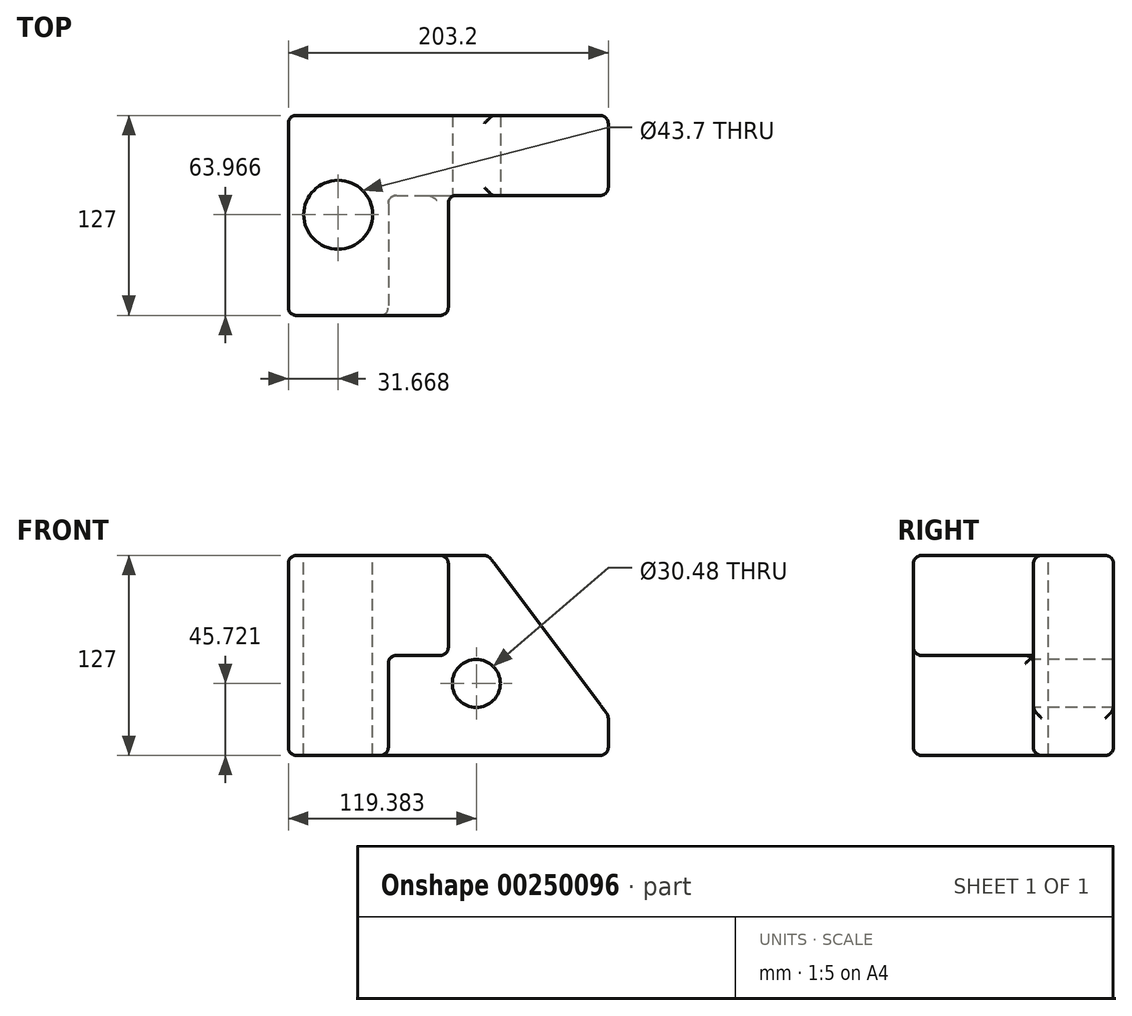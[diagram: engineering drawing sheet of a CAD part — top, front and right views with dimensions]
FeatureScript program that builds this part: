
annotation { "Feature Type Name" : "Feature", "Feature Type Description" : "" }
export const myFeature = defineFeature(function(context is Context, id is Id, definition is map)
    precondition{}
    {
        {
            var Q0;
            Q0=qCreatedBy(makeId("Front.planeOp"),FACE);
            var sketch = newSketch(context, id + "F0", { "sketchPlane" : qUnion([Q0])});
            skLineSegment(sketch, "E0.bottom", {"start": v(-98.38, 50.15) * mm, "end": v(104.82, 50.15) * mm});
            skLineSegment(sketch, "E0.top", {"start": v(-98.38, -76.85) * mm, "end": v(104.82, -76.85) * mm});
            skLineSegment(sketch, "E0.left", {"start": v(-98.38, 50.15) * mm, "end": v(-98.38, -76.85) * mm});
            skLineSegment(sketch, "E0.right", {"start": v(104.82, 50.15) * mm, "end": v(104.82, -76.85) * mm});
            skSolve(sketch);
        }
        {
            var Q0;
            Q0=makeQuery(id+"F0.imprint","IMPRINT",FACE,{"disambiguationData":[TD([[makeQuery(id+"F0.imprint","IMPRINT",EDGE,{"derivedFrom":sQuery(id+"F0.wireOp",EDGE,"E0.bottom")}),-1.0]])]});
            extrude(context, id + "F1", {"entities" : qUnion([Q0]), "depth" : 127 * mm});
        }
        {
            var Q0;
            Q0=makeQuery(id+"F1.opExtrude","CAP_FACE",FACE,{"disambiguationData":[OSD([sQuery(id+"F0.wireOp",EDGE,"E0.bottom"),sQuery(id+"F0.wireOp",EDGE,"E0.top"),sQuery(id+"F0.wireOp",EDGE,"E0.left"),sQuery(id+"F0.wireOp",EDGE,"E0.right")])],"isStart":false});
            var sketch = newSketch(context, id + "F2", { "sketchPlane" : qUnion([Q0])});
            skLineSegment(sketch, "E1", {"start": v(-34.88, -76.85) * mm, "end": v(-34.88, -13.35) * mm});
            skLineSegment(sketch, "E2", {"start": v(-34.88, -13.35) * mm, "end": v(3.22, -13.35) * mm});
            skLineSegment(sketch, "E3", {"start": v(3.22, -13.35) * mm, "end": v(3.22, 50.15) * mm});
            skLineSegment(sketch, "E4", {"start": v(3.22, 50.15) * mm, "end": v(-98.38, 50.15) * mm});
            skLineSegment(sketch, "E5", {"start": v(-98.38, 50.15) * mm, "end": v(-98.38, -76.85) * mm});
            skLineSegment(sketch, "E6", {"start": v(-98.38, -76.85) * mm, "end": v(-34.88, -76.85) * mm});
            skSolve(sketch);
        }
        {
            var Q0;
            {var subQ3=sQuery(id+"F2.wireOp",EDGE,"E1");Q0=makeQuery(id+"F2.imprint","IMPRINT",FACE,{"disambiguationData":[TD([[makeQuery(id+"F2.imprint","IMPRINT",EDGE,{"derivedFrom":subQ3}),-1.0]])]});}
            extrude(context, id + "F3", {"entities" : qUnion([Q0]), "operationType" : NewBodyOperationType.REMOVE, "oppositeDirection" : true, "depth" : 76.2 * mm});
        }
        {
            var Q0;
            Q0=makeQuery(id+"F1.opExtrude","SWEPT_EDGE",EDGE,{"disambiguationData":[OSD([sQuery(id+"F0.wireOp",EDGE,"E0.bottom"),sQuery(id+"F0.wireOp",EDGE,"E0.right")])]});
            chamfer(context, id + "F4", {"entities" : qUnion([Q0]), "chamferType" : ChamferType.TWO_OFFSETS, "width1" : 76.2 * mm, "oppositeDirection" : false, "width2" : 101.6 * mm, "tangentPropagation" : true});
        }
        {
            var Q0;
            Q0=makeQuery(id+"F3.boolean.opBoolean","COPY",EDGE,{"derivedFrom":makeQuery(id+"F3.opExtrude","SWEPT_EDGE",EDGE,{"disambiguationData":[OSD([sQuery(id+"F0.wireOp",EDGE,"E0.bottom"),sQuery(id+"F2.wireOp",EDGE,"E3"),sQuery(id+"F2.wireOp",EDGE,"E4")])]})});
            var Q1;
            Q1=makeQuery(id+"F1.opExtrude","CAP_EDGE",EDGE,{"disambiguationData":[OSD([sQuery(id+"F0.wireOp",EDGE,"E0.bottom")])],"isStart":false});
            var Q2;
            Q2=makeQuery(id+"F1.opExtrude","SWEPT_FACE",FACE,{"disambiguationData":[OSD([sQuery(id+"F0.wireOp",EDGE,"E0.bottom")])]});
            var Q3;
            Q3=makeQuery(id+"F1.opExtrude","CAP_FACE",FACE,{"disambiguationData":[OSD([sQuery(id+"F0.wireOp",EDGE,"E0.bottom"),sQuery(id+"F0.wireOp",EDGE,"E0.top"),sQuery(id+"F0.wireOp",EDGE,"E0.left"),sQuery(id+"F0.wireOp",EDGE,"E0.right")])],"isStart":false});
            var Q4;
            Q4=makeQuery(id+"F3.boolean.opBoolean","COPY",FACE,{"derivedFrom":makeQuery(id+"F3.opExtrude","SWEPT_FACE",FACE,{"disambiguationData":[OSD([sQuery(id+"F2.wireOp",EDGE,"E3")])]})});
            var Q5;
            Q5=makeQuery(id+"F3.boolean.opBoolean","COPY",FACE,{"derivedFrom":makeQuery(id+"F3.opExtrude","SWEPT_FACE",FACE,{"disambiguationData":[OSD([sQuery(id+"F2.wireOp",EDGE,"E1")])]})});
            var Q6;
            Q6=makeQuery(id+"F1.opExtrude","SWEPT_FACE",FACE,{"disambiguationData":[OSD([sQuery(id+"F0.wireOp",EDGE,"E0.right")])]});
            var Q7;
            Q7=makeQuery(id+"F1.opExtrude","SWEPT_FACE",FACE,{"disambiguationData":[OSD([sQuery(id+"F0.wireOp",EDGE,"E0.top")])]});
            var Q8;
            Q8=makeQuery(id+"F1.opExtrude","SWEPT_FACE",FACE,{"disambiguationData":[OSD([sQuery(id+"F0.wireOp",EDGE,"E0.left")])]});
            fillet(context, id + "F5", {"entities" : qUnion([Q0, Q1, Q2, Q3, Q4, Q5, Q6, Q7, Q8]), "radius" : 5.08 * mm, "tangentPropagation" : true, "allowEdgeOverflow" : false});
        }
        {
            var Q0;
            Q0=makeQuery(id+"F3.boolean.opBoolean","COPY",FACE,{"derivedFrom":makeQuery(id+"F3.opExtrude","CAP_FACE",FACE,{"disambiguationData":[OSD([sQuery(id+"F0.wireOp",EDGE,"E0.bottom"),sQuery(id+"F0.wireOp",EDGE,"E0.top"),sQuery(id+"F0.wireOp",EDGE,"E0.right"),sQuery(id+"F2.wireOp",EDGE,"E1"),sQuery(id+"F2.wireOp",EDGE,"E2"),sQuery(id+"F2.wireOp",EDGE,"E3")])],"isStart":false})});
            var sketch = newSketch(context, id + "F6", { "sketchPlane" : qUnion([Q0])});
            skCircle(sketch, "E7", {"center": v(21, -31.13) * mm, "radius": 15.24 * mm});
            skSolve(sketch);
        }
        {
            var Q0;
            Q0=makeQuery(id+"F6.imprint","IMPRINT",FACE,{"disambiguationData":[TD([[makeQuery(id+"F6.imprint","IMPRINT",EDGE,{"derivedFrom":sQuery(id+"F6.wireOp",EDGE,"E7")}),1.0]])]});
            extrude(context, id + "F7", {"entities" : qUnion([Q0]), "operationType" : NewBodyOperationType.REMOVE, "endBound" : BoundingType.THROUGH_ALL, "oppositeDirection" : true, "depth" : 25.4 * mm});
        }
        {
            var Q0;
            Q0=makeQuery(id+"F1.opExtrude","SWEPT_FACE",FACE,{"disambiguationData":[OSD([sQuery(id+"F0.wireOp",EDGE,"E0.bottom")])]});
            var sketch = newSketch(context, id + "F8", { "sketchPlane" : qUnion([Q0])});
            skCircle(sketch, "E8", {"center": v(-66.71, -63.03) * mm, "radius": 21.85 * mm});
            skSolve(sketch);
        }
        {
            var Q0;
            Q0=makeQuery(id+"F8.imprint","IMPRINT",FACE,{"disambiguationData":[TD([[makeQuery(id+"F8.imprint","IMPRINT",EDGE,{"derivedFrom":sQuery(id+"F8.wireOp",EDGE,"E8")}),1.0]])]});
            extrude(context, id + "F9", {"entities" : qUnion([Q0]), "operationType" : NewBodyOperationType.REMOVE, "endBound" : BoundingType.THROUGH_ALL, "oppositeDirection" : true, "depth" : 25.4 * mm});
        }
    });
